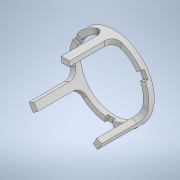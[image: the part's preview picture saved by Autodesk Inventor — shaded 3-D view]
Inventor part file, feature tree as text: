
AUTODESK INVENTOR PART (.ipt)
format: ipt  version: 2020.5 (Build 245400000, 400)  size: 415,232 bytes
history: native  units: mm
features: extrude x3, sketch x3, fillet x1
ambient origin geometry x8: Origin, YZ Plane, XZ Plane, XY Plane, X Axis, Y Axis, Z Axis, Center Point
bodies: Solid1 (feature_tree)
feature tree (7):
  extrude  "Extrusion1"  Depth=2.0mm
  extrude  "Extrusion2"  TaperAngle=120.0deg  [1 undecoded]
  extrude  "Extrusion3"  Depth=3.0mm
  fillet  "Fillet1"  Radius=1.047198mm
  sketch  "Sketch1"  dims[d0=25.0mm d1=2.0mm]
  sketch  "Sketch2"  dims[d2=2.0mm d3=0.0mm d4=120.0deg]
  sketch  "Sketch3"  dims[d5=120.0deg d6=1.047198mm d7=1.047198mm d8=30.0mm d10=360.0deg d12=16.0mm d13=0.0mm d14=1.047198mm d15=1.047198mm d16=30.0mm d18=360.0deg d21=30.0mm d23=30.0mm d24=120.0deg d25=120.0deg d26=1.047198mm d27=1.047198mm d28=360.0deg d29=1.047198mm d30=1.047198mm d31=360.0deg d32=1.0mm d33=0.0mm d34=3.0mm]
note: 1 required parameter value undecoded (feature->parameter linkage not recoverable at this tier; creation-order binding heuristic only, values carry confidence <= 0.55)
